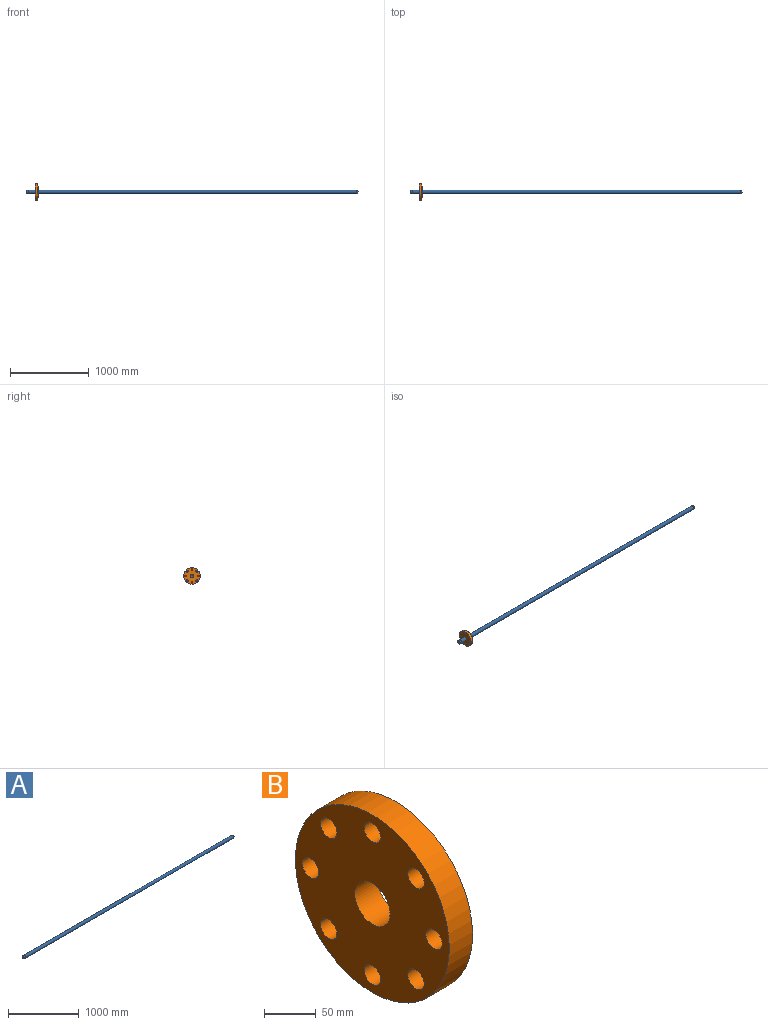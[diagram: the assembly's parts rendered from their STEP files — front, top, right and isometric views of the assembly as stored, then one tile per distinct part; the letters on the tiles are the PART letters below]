
ASSEMBLY  parts=2 mates=1
PART A: 6 faces, bbox 4216.4x48.3x48.3 mm
  f0: plane 45.09x45.09mm, normal (-1,0,0), area 456.4mm2, adj f1,f3
  f1: cylinder r=19.05mm len=4192.27mm, axis (-1,0,0), area 501792.4mm2, adj f0,f2
  f2: sphere r=19.05mm, area 2280.2mm2, adj f1
  f3: cone r=22.54mm half-angle=3.6deg, axis (1,0,0), area 3731.6mm2, adj f0,f5
  f4: sphere r=24.13mm, area 3658.4mm2, adj f5
  f5: cylinder r=24.13mm len=4166.87mm, axis (-1,0,0), area 631752.8mm2, adj f3,f4
PART B: 23 faces, bbox 38.1x209.6x209.6 mm
  f0: plane 128.52x128.52mm, normal (1,0,0), area 11144.3mm2, adj f9,f20
  f1: cylinder r=11.18mm len=38.1mm, axis (-1,0,0), area 2282.7mm2, adj f11,f12,f15,f16,f22
  f2: cylinder r=11.18mm len=38.1mm, axis (-1,0,0), area 2282.7mm2, adj f11,f12,f16,f17,f22
  f3: cylinder r=11.18mm len=38.1mm, axis (-1,0,0), area 2282.7mm2, adj f11,f12,f17,f18,f22
  f4: cylinder r=11.18mm len=38.1mm, axis (-1,0,0), area 2282.7mm2, adj f11,f12,f18,f19,f22
  f5: cylinder r=11.18mm len=38.1mm, axis (-1,0,0), area 2282.7mm2, adj f11,f12,f19,f21,f22
  f6: cylinder r=11.18mm len=38.1mm, axis (-1,0,0), area 2282.7mm2, adj f11,f12,f13,f21,f22
  f7: cylinder r=11.18mm len=38.1mm, axis (-1,0,0), area 2282.7mm2, adj f11,f12,f13,f14,f22
  f8: cylinder r=11.18mm len=38.1mm, axis (-1,0,0), area 2282.7mm2, adj f11,f12,f14,f15,f22
  f9: cylinder r=24.13mm len=48.26mm, axis (-1,0,0), area 4813.7mm2, adj f0,f12
  f10: cylinder r=104.77mm len=209.55mm, axis (-1,0,0), area 20901.7mm2, adj f11,f12
  f11: plane 209.55x209.55mm, normal (1,0,0), area 14283.2mm2, adj f1,f2,f3,f4,f5,f6,f7,f8
  f12: plane 209.55x209.55mm, normal (-1,0,0), area 29519.4mm2, adj f1,f2,f3,f4,f5,f6,f7,f8
  f13: cylinder r=73.79mm len=45.11mm, axis (-1,0,0), area 316mm2, adj f6,f7,f11,f22
  f14: cylinder r=73.79mm len=45.11mm, axis (-1,0,0), area 316mm2, adj f7,f8,f11,f22
  f15: cylinder r=73.79mm len=45.11mm, axis (-1,0,0), area 316mm2, adj f1,f8,f11,f22
  f16: cylinder r=73.79mm len=45.11mm, axis (-1,0,0), area 316mm2, adj f1,f2,f11,f22
  f17: cylinder r=73.79mm len=45.11mm, axis (-1,0,0), area 316mm2, adj f2,f3,f11,f22
  f18: cylinder r=73.79mm len=45.11mm, axis (-1,0,0), area 316mm2, adj f3,f4,f11,f22
  f19: cylinder r=73.79mm len=45.11mm, axis (-1,0,0), area 316mm2, adj f4,f5,f11,f22
  f20: cylinder r=64.26mm len=128.52mm, axis (-1,0,0), area 2563.9mm2, adj f0,f22
  f21: cylinder r=73.79mm len=45.11mm, axis (-1,0,0), area 316mm2, adj f5,f6,f11,f22
  f22: plane 147.35x147.35mm, normal (1,0,0), area 4091.9mm2, adj f1,f2,f3,f4,f5,f6,f7,f8
PLACE A at identity
PLACE B t=(114.3,240.26,-50.62)mm
MATE planar A.f1 <-> B.f9  axis (1,0,0) through (4216.4,0,0)mm
